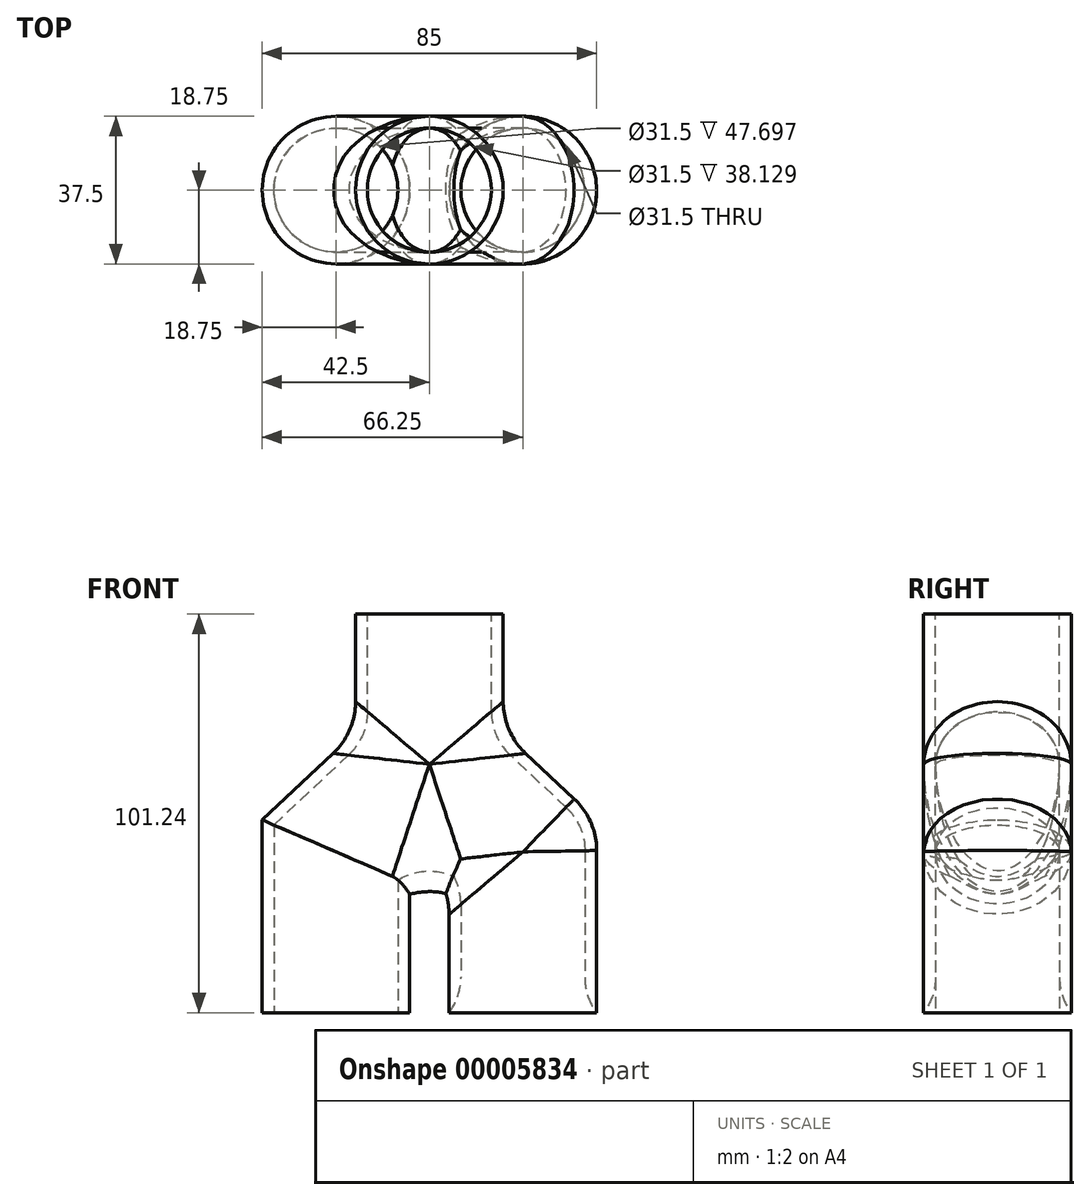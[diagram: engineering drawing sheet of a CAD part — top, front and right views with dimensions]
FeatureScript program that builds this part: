
annotation { "Feature Type Name" : "Feature", "Feature Type Description" : "" }
export const myFeature = defineFeature(function(context is Context, id is Id, definition is map)
    precondition{}
    {
        {
            var Q0;
            Q0=qCreatedBy(makeId("Front.planeOp"),FACE);
            var sketch = newSketch(context, id + "F0", { "sketchPlane" : qUnion([Q0])});
            skLineSegment(sketch, "E0.bottom", {"start": v(-18.75, 66.56) * mm, "end": v(-15.75, 66.56) * mm});
            skLineSegment(sketch, "E0.left", {"start": v(-18.75, 66.56) * mm, "end": v(-18.75, 14.77) * mm});
            skLineSegment(sketch, "E1.top", {"start": v(-42.5, -34.68) * mm, "end": v(-39.5, -34.68) * mm});
            skLineSegment(sketch, "E1.left", {"start": v(-42.5, 14.32) * mm, "end": v(-42.5, -34.68) * mm});
            skLineSegment(sketch, "E1.right", {"start": v(-5, -4.68) * mm, "end": v(-5, -34.68) * mm});
            skLineSegment(sketch, "E2", {"start": v(0, 69.18) * mm, "end": v(0, -67.25) * mm, "construction": true});
            skLineSegment(sketch, "E3.0", {"start": v(-39.5, 13.01) * mm, "end": v(-39.5, -34.68) * mm});
            skLineSegment(sketch, "E3.1", {"start": v(-39.5, 13.01) * mm, "end": v(-15.75, 35.26) * mm});
            skLineSegment(sketch, "E3.2", {"start": v(-15.75, 66.56) * mm, "end": v(-15.75, 14.77) * mm});
            skLineSegment(sketch, "E4.0", {"start": v(-8, -0.64) * mm, "end": v(-8, -34.68) * mm});
            skLineSegment(sketch, "E5", {"start": v(-3.42, 3.65) * mm, "end": v(-8, -0.64) * mm});
            skLineSegment(sketch, "E6", {"start": v(-5, -4.68) * mm, "end": v(0, 0) * mm});
            skArc(sketch, "E7", {"start": v(0, 5) * mm, "mid": v(-1.84, 4.65) * mm, "end": v(-3.42, 3.65) * mm});
            skLineSegment(sketch, "E8.trimOffspring", {"start": v(-8, -34.68) * mm, "end": v(-5, -34.68) * mm});
            skLineSegment(sketch, "E9.MirrorCS", {"start": v(8, -34.68) * mm, "end": v(5, -34.68) * mm});
            skLineSegment(sketch, "E10.MirrorCS", {"start": v(42.5, -34.68) * mm, "end": v(39.5, -34.68) * mm});
            skLineSegment(sketch, "E11.MirrorCS", {"start": v(18.75, 66.56) * mm, "end": v(15.75, 66.56) * mm});
            skArc(sketch, "E12.MirrorCS", {"start": v(0, 5) * mm, "mid": v(1.84, 4.65) * mm, "end": v(3.42, 3.65) * mm});
            skLineSegment(sketch, "E13.MirrorCS", {"start": v(3.42, 3.65) * mm, "end": v(8, -0.64) * mm});
            skLineSegment(sketch, "E14.MirrorCS", {"start": v(8, -0.64) * mm, "end": v(8, -34.68) * mm});
            skLineSegment(sketch, "E15.MirrorCS", {"start": v(15.75, 66.56) * mm, "end": v(15.75, 35.26) * mm});
            skLineSegment(sketch, "E16.MirrorCS", {"start": v(39.5, 13.01) * mm, "end": v(15.75, 35.26) * mm});
            skLineSegment(sketch, "E17.MirrorCS", {"start": v(42.5, 14.32) * mm, "end": v(18.75, 36.56) * mm});
            skLineSegment(sketch, "E18.MirrorCS", {"start": v(5, -4.68) * mm, "end": v(5, -34.68) * mm});
            skLineSegment(sketch, "E19.MirrorCS", {"start": v(42.5, 14.32) * mm, "end": v(42.5, -34.68) * mm});
            skLineSegment(sketch, "E20.MirrorCS", {"start": v(18.75, 66.56) * mm, "end": v(18.75, 36.56) * mm});
            skLineSegment(sketch, "E21.MirrorCS", {"start": v(5, -4.68) * mm, "end": v(0, 0) * mm});
            skLineSegment(sketch, "E22.MirrorCS", {"start": v(39.5, 13.01) * mm, "end": v(39.5, -34.68) * mm});
            skLineSegment(sketch, "E23", {"start": v(0, 0) * mm, "end": v(0, 5) * mm});
            skLineSegment(sketch, "E24", {"start": v(0, 28.43) * mm, "end": v(-56.58, -24.56) * mm, "construction": true});
            skLineSegment(sketch, "E25", {"start": v(0, 28.43) * mm, "end": v(56.54, -24.52) * mm, "construction": true});
            skLineSegment(sketch, "E26", {"start": v(3.42, 3.65) * mm, "end": v(14.18, 15.15) * mm, "construction": true});
            skLineSegment(sketch, "E27", {"start": v(14.18, 15.15) * mm, "end": v(24.95, 26.64) * mm, "construction": true});
            skPoint(sketch, "E28", {"position": v(0, 28.43) * mm});
            skLineSegment(sketch, "E29", {"start": v(-39.5, 13.01) * mm, "end": v(-42.5, 14.32) * mm});
            skLineSegment(sketch, "E30", {"start": v(15.75, 35.26) * mm, "end": v(18.75, 36.56) * mm});
            skLineSegment(sketch, "E31", {"start": v(39.5, 13.01) * mm, "end": v(42.5, 14.32) * mm});
            skLineSegment(sketch, "E32", {"start": v(-23.75, -34.68) * mm, "end": v(-23.75, 15.83) * mm, "construction": true});
            skLineSegment(sketch, "E33", {"start": v(-39.5, -34.68) * mm, "end": v(-23.75, -34.68) * mm, "construction": true});
            skLineSegment(sketch, "E34", {"start": v(-23.75, -34.68) * mm, "end": v(-8, -34.68) * mm, "construction": true});
            skLineSegment(sketch, "E35.MirrorCS", {"start": v(-47.5, 69.18) * mm, "end": v(-47.5, -67.25) * mm, "construction": true});
            skLineSegment(sketch, "E36", {"start": v(8, -34.68) * mm, "end": v(23.75, -34.68) * mm, "construction": true});
            skLineSegment(sketch, "E37", {"start": v(23.75, -34.68) * mm, "end": v(39.5, -34.68) * mm, "construction": true});
            skLineSegment(sketch, "E38", {"start": v(23.75, -34.68) * mm, "end": v(23.75, 14.7) * mm, "construction": true});
            skLineSegment(sketch, "E39", {"start": v(-18.75, 14.77) * mm, "end": v(-15.75, 14.77) * mm});
            skLineSegment(sketch, "E40", {"start": v(-42.5, 14.32) * mm, "end": v(-9.1, 45.59) * mm});
            skLineSegment(sketch, "E41", {"start": v(-9.1, 45.59) * mm, "end": v(-7.06, 43.4) * mm});
            skLineSegment(sketch, "E42", {"start": v(-7.06, 43.4) * mm, "end": v(-15.75, 35.26) * mm});
            skLineSegment(sketch, "E43.MirrorCS", {"start": v(9.1, 45.59) * mm, "end": v(7.06, 43.4) * mm});
            skLineSegment(sketch, "E44.MirrorCS", {"start": v(7.06, 43.4) * mm, "end": v(15.75, 35.26) * mm});
            skLineSegment(sketch, "E45.MirrorCS", {"start": v(42.5, 14.32) * mm, "end": v(9.1, 45.59) * mm});
            skSolve(sketch);
        }
        {
            var Q0;
            Q0=makeQuery(id+"F0.imprint","IMPRINT",FACE,{"disambiguationData":[TD([[makeQuery(id+"F0.imprint","IMPRINT",EDGE,{"derivedFrom":sQuery(id+"F0.wireOp",EDGE,"E0.bottom")}),-1.0]])]});
            var Q1;
            {var subQ0=sQuery(id+"F0.wireOp",EDGE,"xYfYZVj4-OU23-bML6-88x0-pwoqxrOmsgBR");Q1=makeQuery(id+"F0.imprint","IMPRINT",FACE,{"disambiguationData":[TD([[makeQuery(id+"F0.imprint","IMPRINT",EDGE,{"derivedFrom":subQ0}),-1.0]])]});}
            var Q2;
            {var subQ0=sQuery(id+"F0.wireOp",EDGE,"E39");Q2=makeQuery(id+"F0.imprint","IMPRINT",FACE,{"disambiguationData":[TD([[makeQuery(id+"F0.imprint","IMPRINT",EDGE,{"derivedFrom":subQ0}),1.0]])]});}
            var Q3;
            {var subQ0=sQuery(id+"F0.wireOp",EDGE,"E40");var subQ1=sQuery(id+"F0.wireOp",EDGE,"E0.left");var subQ2=makeQuery(id+"F0.imprint","INTERSECT",VERTEX,{"derivedFrom":[subQ1,subQ0]});Q3=makeQuery(id+"F0.imprint","IMPRINT",FACE,{"disambiguationData":[TD([[makeQuery(id+"F0.imprint","IMPRINT",EDGE,{"disambiguationData":[TD([[subQ2,-1.0]])],"derivedFrom":subQ1}),1.0]])]});}
            var Q4;
            Q4=sQuery(id+"F0.wireOp",EDGE,"E2");
            revolve(context, id + "F1", {"surfaceOperationType" : NewSurfaceOperationType.NEW, "entities" : qUnion([Q0, Q1, Q2, Q3]), "axis" : qUnion([Q4]), "revolveType" : RevolveType.FULL});
        }
        {
            var Q0;
            {var subQ5=sQuery(id+"F0.wireOp",EDGE,"E29");Q0=makeQuery(id+"F0.imprint","IMPRINT",FACE,{"disambiguationData":[TD([[makeQuery(id+"F0.imprint","IMPRINT",EDGE,{"derivedFrom":subQ5}),-1.0]])]});}
            var Q1;
            {var subQ0=sQuery(id+"F0.wireOp",EDGE,"E40");var subQ1=sQuery(id+"F0.wireOp",EDGE,"E0.left");var subQ2=makeQuery(id+"F0.imprint","INTERSECT",VERTEX,{"derivedFrom":[subQ1,subQ0]});Q1=makeQuery(id+"F0.imprint","IMPRINT",FACE,{"disambiguationData":[TD([[makeQuery(id+"F0.imprint","IMPRINT",EDGE,{"disambiguationData":[TD([[subQ2,-1.0]])],"derivedFrom":subQ1}),1.0]])]});}
            var Q2;
            {var subQ4=sQuery(id+"F0.wireOp",EDGE,"E41");Q2=makeQuery(id+"F0.imprint","IMPRINT",FACE,{"disambiguationData":[TD([[makeQuery(id+"F0.imprint","IMPRINT",EDGE,{"derivedFrom":subQ4}),-1.0]])]});}
            var Q3;
            Q3=sQuery(id+"F0.wireOp",EDGE,"E24");
            revolve(context, id + "F2", {"surfaceOperationType" : NewSurfaceOperationType.NEW, "entities" : qUnion([Q0, Q1, Q2]), "axis" : qUnion([Q3]), "revolveType" : RevolveType.FULL});
        }
        {
            var Q0;
            Q0=makeQuery(id+"F0.imprint","IMPRINT",FACE,{"disambiguationData":[TD([[makeQuery(id+"F0.imprint","IMPRINT",EDGE,{"derivedFrom":sQuery(id+"F0.wireOp",EDGE,"E1.top")}),1.0]])]});
            var Q1;
            Q1=sQuery(id+"F0.wireOp",EDGE,"E32");
            revolve(context, id + "F3", {"surfaceOperationType" : NewSurfaceOperationType.NEW, "entities" : qUnion([Q0]), "axis" : qUnion([Q1]), "revolveType" : RevolveType.FULL});
        }
        {
            var Q0;
            Q0=qCreatedBy(makeId("Front.planeOp"),FACE);
            var sketch = newSketch(context, id + "F4", { "sketchPlane" : qUnion([Q0])});
            skPoint(sketch, "E46.0", {"position": v(-42.5, 14.32) * mm});
            skLineSegment(sketch, "E47.0", {"start": v(-5, -1.94) * mm, "end": v(-5, -34.68) * mm});
            skPoint(sketch, "E48.orphan", {"position": v(-5, -4.68) * mm});
            skLineSegment(sketch, "E49", {"start": v(-5, -1.94) * mm, "end": v(-42.5, 14.32) * mm});
            skLineSegment(sketch, "E50", {"start": v(-42.5, 14.32) * mm, "end": v(-42.5, -34.68) * mm});
            skLineSegment(sketch, "E51", {"start": v(-42.5, -34.68) * mm, "end": v(-5, -34.68) * mm});
            skLineSegment(sketch, "E52.0", {"start": v(-42.5, 14.32) * mm, "end": v(-18.75, 36.56) * mm});
            skLineSegment(sketch, "E53.0", {"start": v(-18.75, 66.56) * mm, "end": v(-18.75, 36.56) * mm});
            skLineSegment(sketch, "E54.0", {"start": v(13.72, 15.58) * mm, "end": v(14.58, 14.77) * mm});
            skLineSegment(sketch, "E55", {"start": v(-18.75, 36.56) * mm, "end": v(0, 28.43) * mm});
            skLineSegment(sketch, "E56.0", {"start": v(18.75, 66.56) * mm, "end": v(18.75, 36.56) * mm});
            skLineSegment(sketch, "E57", {"start": v(0, 28.43) * mm, "end": v(18.75, 36.56) * mm});
            skPoint(sketch, "E58.orphan", {"position": v(-9.1, 45.59) * mm});
            skLineSegment(sketch, "E59.0", {"start": v(-18.75, 66.56) * mm, "end": v(18.75, 66.56) * mm});
            skLineSegment(sketch, "E60", {"start": v(-18.75, 36.56) * mm, "end": v(-18.75, 66.56) * mm});
            skPoint(sketch, "E61.0.start.orphan", {"position": v(0, 28.43) * mm});
            skPoint(sketch, "E62.orphan", {"position": v(56.54, -24.52) * mm});
            skPoint(sketch, "E63.orphan", {"position": v(0, -67.25) * mm});
            skLineSegment(sketch, "E64.trimOffspring", {"start": v(0, 28.43) * mm, "end": v(0, 2.74) * mm});
            skLineSegment(sketch, "E65.trimOffspring", {"start": v(0, 2.74) * mm, "end": v(-5, -1.94) * mm});
            skPoint(sketch, "E66.0.start.orphan", {"position": v(0, 69.18) * mm});
            skSolve(sketch);
        }
        {
            var Q0;
            Q0=makeQuery(id+"F4.imprint","IMPRINT",FACE,{"disambiguationData":[TD([[makeQuery(id+"F4.imprint","IMPRINT",EDGE,{"derivedFrom":sQuery(id+"F4.wireOp",EDGE,"E55")}),1.0]])]});
            extrude(context, id + "F5", {"entities" : qUnion([Q0]), "endBound" : BoundingType.SYMMETRIC, "depth" : 40 * mm, "offsetDistance" : 25 * mm});
        }
        {
            var Q0;
            Q0=makeQuery(id+"F4.imprint","IMPRINT",FACE,{"disambiguationData":[TD([[makeQuery(id+"F4.imprint","IMPRINT",EDGE,{"derivedFrom":sQuery(id+"F4.wireOp",EDGE,"E49")}),-1.0]])]});
            extrude(context, id + "F6", {"entities" : qUnion([Q0]), "endBound" : BoundingType.SYMMETRIC, "depth" : 40 * mm, "offsetDistance" : 25 * mm});
        }
        {
            var Q0;
            Q0=makeQuery(id+"F4.imprint","IMPRINT",FACE,{"disambiguationData":[TD([[makeQuery(id+"F4.imprint","IMPRINT",EDGE,{"derivedFrom":sQuery(id+"F4.wireOp",EDGE,"E47.0")}),-1.0]])]});
            extrude(context, id + "F7", {"entities" : qUnion([Q0]), "endBound" : BoundingType.SYMMETRIC, "depth" : 40 * mm, "offsetDistance" : 25 * mm});
        }
        {
            var Q0;
            Q0=makeQuery(id+"F1.opRevolve","SWEPT_BODY",BODY,{"disambiguationData":[OSD([sQuery(id+"F0.wireOp",EDGE,"E0.bottom"),sQuery(id+"F0.wireOp",EDGE,"E0.left"),sQuery(id+"F0.wireOp",EDGE,"E3.2"),sQuery(id+"F0.wireOp",EDGE,"E39")])]});
            var Q1;
            Q1=makeQuery(id+"F5.opExtrude","SWEPT_BODY",BODY,{"disambiguationData":[OSD([sQuery(id+"F4.wireOp",EDGE,"E55"),sQuery(id+"F4.wireOp",EDGE,"E56.0"),sQuery(id+"F4.wireOp",EDGE,"E57"),sQuery(id+"F4.wireOp",EDGE,"E59.0"),sQuery(id+"F4.wireOp",EDGE,"E60")])]});
            booleanBodies(context, id + "F8", {"operationType" : BooleanOperationType.INTERSECTION, "tools" : qUnion([Q0, Q1])});
        }
        {
            var Q0;
            Q0=makeQuery(id+"F6.opExtrude","SWEPT_BODY",BODY,{"disambiguationData":[OSD([sQuery(id+"F4.wireOp",EDGE,"E49"),sQuery(id+"F4.wireOp",EDGE,"E52.0"),sQuery(id+"F4.wireOp",EDGE,"E55"),sQuery(id+"F4.wireOp",EDGE,"E64.trimOffspring"),sQuery(id+"F4.wireOp",EDGE,"E65.trimOffspring")])]});
            var Q1;
            Q1=makeQuery(id+"F2.opRevolve","SWEPT_BODY",BODY,{"disambiguationData":[OSD([sQuery(id+"F0.wireOp",EDGE,"E3.1"),sQuery(id+"F0.wireOp",EDGE,"E29"),sQuery(id+"F0.wireOp",EDGE,"E40"),sQuery(id+"F0.wireOp",EDGE,"E41"),sQuery(id+"F0.wireOp",EDGE,"E42")])]});
            booleanBodies(context, id + "F9", {"operationType" : BooleanOperationType.INTERSECTION, "tools" : qUnion([Q0, Q1])});
        }
        {
            var Q0;
            Q0=makeQuery(id+"F3.opRevolve","SWEPT_BODY",BODY,{"disambiguationData":[OSD([sQuery(id+"F0.wireOp",EDGE,"E1.top"),sQuery(id+"F0.wireOp",EDGE,"E1.left"),sQuery(id+"F0.wireOp",EDGE,"E3.0"),sQuery(id+"F0.wireOp",EDGE,"E29")])]});
            var Q1;
            Q1=makeQuery(id+"F7.opExtrude","SWEPT_BODY",BODY,{"disambiguationData":[OSD([sQuery(id+"F4.wireOp",EDGE,"E47.0"),sQuery(id+"F4.wireOp",EDGE,"E49"),sQuery(id+"F4.wireOp",EDGE,"E50"),sQuery(id+"F4.wireOp",EDGE,"E51")])]});
            booleanBodies(context, id + "F10", {"operationType" : BooleanOperationType.INTERSECTION, "tools" : qUnion([Q0, Q1])});
        }
        {
            var Q0;
            Q0=makeQuery(id+"F9.opBoolean","INTERSECT",BODY,{"derivedFrom":[makeQuery(id+"F2.opRevolve","SWEPT_BODY",BODY,{"disambiguationData":[OSD([sQuery(id+"F0.wireOp",EDGE,"E3.1"),sQuery(id+"F0.wireOp",EDGE,"E29"),sQuery(id+"F0.wireOp",EDGE,"E40"),sQuery(id+"F0.wireOp",EDGE,"E41"),sQuery(id+"F0.wireOp",EDGE,"E42")])]}),makeQuery(id+"F6.opExtrude","SWEPT_BODY",BODY,{"disambiguationData":[OSD([sQuery(id+"F4.wireOp",EDGE,"E49"),sQuery(id+"F4.wireOp",EDGE,"E52.0"),sQuery(id+"F4.wireOp",EDGE,"E55"),sQuery(id+"F4.wireOp",EDGE,"E64.trimOffspring"),sQuery(id+"F4.wireOp",EDGE,"E65.trimOffspring")])]})]});
            var Q1;
            Q1=qCreatedBy(makeId("Right.planeOp"),FACE);
            mirror(context, id + "F11", {"entities" : qUnion([Q0]), "mirrorPlane" : qUnion([Q1])});
        }
        {
            var Q0;
            Q0=makeQuery(id+"F10.opBoolean","INTERSECT",BODY,{"derivedFrom":[makeQuery(id+"F3.opRevolve","SWEPT_BODY",BODY,{"disambiguationData":[OSD([sQuery(id+"F0.wireOp",EDGE,"E1.top"),sQuery(id+"F0.wireOp",EDGE,"E1.left"),sQuery(id+"F0.wireOp",EDGE,"E3.0"),sQuery(id+"F0.wireOp",EDGE,"E29")])]}),makeQuery(id+"F7.opExtrude","SWEPT_BODY",BODY,{"disambiguationData":[OSD([sQuery(id+"F4.wireOp",EDGE,"E47.0"),sQuery(id+"F4.wireOp",EDGE,"E49"),sQuery(id+"F4.wireOp",EDGE,"E50"),sQuery(id+"F4.wireOp",EDGE,"E51")])]})]});
            var Q1;
            Q1=qCreatedBy(makeId("Right.planeOp"),FACE);
            mirror(context, id + "F12", {"operationType" : NewBodyOperationType.ADD, "entities" : qUnion([Q0]), "mirrorPlane" : qUnion([Q1])});
        }
        {
            var Q0;
            Q0=makeQuery(id+"F9.opBoolean","INTERSECT",BODY,{"derivedFrom":[makeQuery(id+"F2.opRevolve","SWEPT_BODY",BODY,{"disambiguationData":[OSD([sQuery(id+"F0.wireOp",EDGE,"E3.1"),sQuery(id+"F0.wireOp",EDGE,"E29"),sQuery(id+"F0.wireOp",EDGE,"E40"),sQuery(id+"F0.wireOp",EDGE,"E41"),sQuery(id+"F0.wireOp",EDGE,"E42")])]}),makeQuery(id+"F6.opExtrude","SWEPT_BODY",BODY,{"disambiguationData":[OSD([sQuery(id+"F4.wireOp",EDGE,"E49"),sQuery(id+"F4.wireOp",EDGE,"E52.0"),sQuery(id+"F4.wireOp",EDGE,"E55"),sQuery(id+"F4.wireOp",EDGE,"E64.trimOffspring"),sQuery(id+"F4.wireOp",EDGE,"E65.trimOffspring")])]})]});
            var Q1;
            Q1=makeQuery(id+"F10.opBoolean","INTERSECT",BODY,{"derivedFrom":[makeQuery(id+"F3.opRevolve","SWEPT_BODY",BODY,{"disambiguationData":[OSD([sQuery(id+"F0.wireOp",EDGE,"E1.top"),sQuery(id+"F0.wireOp",EDGE,"E1.left"),sQuery(id+"F0.wireOp",EDGE,"E3.0"),sQuery(id+"F0.wireOp",EDGE,"E29")])]}),makeQuery(id+"F7.opExtrude","SWEPT_BODY",BODY,{"disambiguationData":[OSD([sQuery(id+"F4.wireOp",EDGE,"E47.0"),sQuery(id+"F4.wireOp",EDGE,"E49"),sQuery(id+"F4.wireOp",EDGE,"E50"),sQuery(id+"F4.wireOp",EDGE,"E51")])]})]});
            var Q2;
            Q2=makeQuery(id+"F8.opBoolean","INTERSECT",BODY,{"derivedFrom":[makeQuery(id+"F1.opRevolve","SWEPT_BODY",BODY,{"disambiguationData":[OSD([sQuery(id+"F0.wireOp",EDGE,"E0.bottom"),sQuery(id+"F0.wireOp",EDGE,"E0.left"),sQuery(id+"F0.wireOp",EDGE,"E3.2"),sQuery(id+"F0.wireOp",EDGE,"E39")])]}),makeQuery(id+"F5.opExtrude","SWEPT_BODY",BODY,{"disambiguationData":[OSD([sQuery(id+"F4.wireOp",EDGE,"E55"),sQuery(id+"F4.wireOp",EDGE,"E56.0"),sQuery(id+"F4.wireOp",EDGE,"E57"),sQuery(id+"F4.wireOp",EDGE,"E59.0"),sQuery(id+"F4.wireOp",EDGE,"E60")])]})]});
            var Q3;
            Q3=makeQuery(id+"F11.opPattern","COPY",BODY,{"derivedFrom":makeQuery(id+"F9.opBoolean","INTERSECT",BODY,{"derivedFrom":[makeQuery(id+"F2.opRevolve","SWEPT_BODY",BODY,{"disambiguationData":[OSD([sQuery(id+"F0.wireOp",EDGE,"E3.1"),sQuery(id+"F0.wireOp",EDGE,"E29"),sQuery(id+"F0.wireOp",EDGE,"E40"),sQuery(id+"F0.wireOp",EDGE,"E41"),sQuery(id+"F0.wireOp",EDGE,"E42")])]}),makeQuery(id+"F6.opExtrude","SWEPT_BODY",BODY,{"disambiguationData":[OSD([sQuery(id+"F4.wireOp",EDGE,"E49"),sQuery(id+"F4.wireOp",EDGE,"E52.0"),sQuery(id+"F4.wireOp",EDGE,"E55"),sQuery(id+"F4.wireOp",EDGE,"E64.trimOffspring"),sQuery(id+"F4.wireOp",EDGE,"E65.trimOffspring")])]})]}),"instanceName":"1"});
            booleanBodies(context, id + "F13", {"operationType" : BooleanOperationType.UNION, "tools" : qUnion([Q0, Q1, Q2, Q3])});
        }
        {
            var Q0;
            {var subQ0=sQuery(id+"F4.wireOp",EDGE,"E49");Q0=makeQuery(id+"F13.opBoolean","MERGE",EDGE,{"derivedFrom":[makeQuery(id+"F9.opBoolean","INTERSECT",EDGE,{"derivedFrom":[makeQuery(id+"F2.opRevolve","SWEPT_FACE",FACE,{"disambiguationData":[OSD([sQuery(id+"F0.wireOp",EDGE,"E40")])]}),makeQuery(id+"F6.opExtrude","SWEPT_FACE",FACE,{"disambiguationData":[OSD([subQ0])]})]}),makeQuery(id+"F10.opBoolean","INTERSECT",EDGE,{"derivedFrom":[makeQuery(id+"F3.opRevolve","SWEPT_FACE",FACE,{"disambiguationData":[OSD([sQuery(id+"F0.wireOp",EDGE,"E1.left")])]}),makeQuery(id+"F7.opExtrude","SWEPT_FACE",FACE,{"disambiguationData":[OSD([subQ0])]})]})]});}
            var Q1;
            {var subQ0=sQuery(id+"F4.wireOp",EDGE,"E49");Q1=makeQuery(id+"F12.boolean.opBoolean","MERGE",EDGE,{"derivedFrom":[makeQuery(id+"F11.opPattern","COPY",EDGE,{"derivedFrom":makeQuery(id+"F9.opBoolean","INTERSECT",EDGE,{"derivedFrom":[makeQuery(id+"F2.opRevolve","SWEPT_FACE",FACE,{"disambiguationData":[OSD([sQuery(id+"F0.wireOp",EDGE,"E40")])]}),makeQuery(id+"F6.opExtrude","SWEPT_FACE",FACE,{"disambiguationData":[OSD([subQ0])]})]}),"instanceName":"1"}),makeQuery(id+"F12.opPattern","COPY",EDGE,{"derivedFrom":makeQuery(id+"F10.opBoolean","INTERSECT",EDGE,{"derivedFrom":[makeQuery(id+"F3.opRevolve","SWEPT_FACE",FACE,{"disambiguationData":[OSD([sQuery(id+"F0.wireOp",EDGE,"E1.left")])]}),makeQuery(id+"F7.opExtrude","SWEPT_FACE",FACE,{"disambiguationData":[OSD([subQ0])]})]}),"instanceName":"1"})]});}
            var Q2;
            Q2=makeQuery(id+"F13.opBoolean","MERGE",EDGE,{"derivedFrom":[makeQuery(id+"F8.opBoolean","INTERSECT",EDGE,{"derivedFrom":[makeQuery(id+"F1.opRevolve","SWEPT_FACE",FACE,{"disambiguationData":[OSD([sQuery(id+"F0.wireOp",EDGE,"E0.left")])]}),makeQuery(id+"F5.opExtrude","SWEPT_FACE",FACE,{"disambiguationData":[OSD([sQuery(id+"F4.wireOp",EDGE,"E57")])]})]}),makeQuery(id+"F11.opPattern","COPY",EDGE,{"derivedFrom":makeQuery(id+"F9.opBoolean","INTERSECT",EDGE,{"derivedFrom":[makeQuery(id+"F2.opRevolve","SWEPT_FACE",FACE,{"disambiguationData":[OSD([sQuery(id+"F0.wireOp",EDGE,"E40")])]}),makeQuery(id+"F6.opExtrude","SWEPT_FACE",FACE,{"disambiguationData":[OSD([sQuery(id+"F4.wireOp",EDGE,"E55")])]})]}),"instanceName":"1"})]});
            var Q3;
            {var subQ0=sQuery(id+"F4.wireOp",EDGE,"E55");Q3=makeQuery(id+"F13.opBoolean","MERGE",EDGE,{"derivedFrom":[makeQuery(id+"F8.opBoolean","INTERSECT",EDGE,{"derivedFrom":[makeQuery(id+"F1.opRevolve","SWEPT_FACE",FACE,{"disambiguationData":[OSD([sQuery(id+"F0.wireOp",EDGE,"E0.left")])]}),makeQuery(id+"F5.opExtrude","SWEPT_FACE",FACE,{"disambiguationData":[OSD([subQ0])]})]}),makeQuery(id+"F9.opBoolean","INTERSECT",EDGE,{"derivedFrom":[makeQuery(id+"F2.opRevolve","SWEPT_FACE",FACE,{"disambiguationData":[OSD([sQuery(id+"F0.wireOp",EDGE,"E40")])]}),makeQuery(id+"F6.opExtrude","SWEPT_FACE",FACE,{"disambiguationData":[OSD([subQ0])]})]})]});}
            var Q4;
            {var subQ0=makeQuery(id+"F9.opBoolean","INTERSECT",EDGE,{"derivedFrom":[makeQuery(id+"F2.opRevolve","SWEPT_FACE",FACE,{"disambiguationData":[OSD([sQuery(id+"F0.wireOp",EDGE,"E40")])]}),makeQuery(id+"F6.opExtrude","SWEPT_FACE",FACE,{"disambiguationData":[OSD([sQuery(id+"F4.wireOp",EDGE,"E64.trimOffspring")])]})]});Q4=makeQuery(id+"F13.opBoolean","MERGE",EDGE,{"derivedFrom":[subQ0,makeQuery(id+"F11.opPattern","COPY",EDGE,{"derivedFrom":subQ0,"instanceName":"1"})]});}
            fillet(context, id + "F14", {"entities" : qUnion([Q0, Q1, Q2, Q3, Q4]), "radius" : 18 * mm, "tangentPropagation" : true, "allowEdgeOverflow" : false});
        }
        {
            var Q0;
            {var subQ0=sQuery(id+"F4.wireOp",EDGE,"E49");Q0=makeQuery(id+"F13.opBoolean","MERGE",EDGE,{"derivedFrom":[makeQuery(id+"F9.opBoolean","INTERSECT",EDGE,{"derivedFrom":[makeQuery(id+"F2.opRevolve","SWEPT_FACE",FACE,{"disambiguationData":[OSD([sQuery(id+"F0.wireOp",EDGE,"E3.1"),sQuery(id+"F0.wireOp",EDGE,"E42")])]}),makeQuery(id+"F6.opExtrude","SWEPT_FACE",FACE,{"disambiguationData":[OSD([subQ0])]})]}),makeQuery(id+"F10.opBoolean","INTERSECT",EDGE,{"derivedFrom":[makeQuery(id+"F3.opRevolve","SWEPT_FACE",FACE,{"disambiguationData":[OSD([sQuery(id+"F0.wireOp",EDGE,"E3.0")])]}),makeQuery(id+"F7.opExtrude","SWEPT_FACE",FACE,{"disambiguationData":[OSD([subQ0])]})]})]});}
            var Q1;
            Q1=makeQuery(id+"F12.opPattern","COPY",FACE,{"derivedFrom":makeQuery(id+"F3.opRevolve","SWEPT_FACE",FACE,{"disambiguationData":[OSD([sQuery(id+"F0.wireOp",EDGE,"E3.0")])]}),"instanceName":"1"});
            var Q2;
            {var subQ0=sQuery(id+"F4.wireOp",EDGE,"E55");Q2=makeQuery(id+"F13.opBoolean","MERGE",EDGE,{"derivedFrom":[makeQuery(id+"F8.opBoolean","INTERSECT",EDGE,{"derivedFrom":[makeQuery(id+"F1.opRevolve","SWEPT_FACE",FACE,{"disambiguationData":[OSD([sQuery(id+"F0.wireOp",EDGE,"E3.2")])]}),makeQuery(id+"F5.opExtrude","SWEPT_FACE",FACE,{"disambiguationData":[OSD([subQ0])]})]}),makeQuery(id+"F9.opBoolean","INTERSECT",EDGE,{"derivedFrom":[makeQuery(id+"F2.opRevolve","SWEPT_FACE",FACE,{"disambiguationData":[OSD([sQuery(id+"F0.wireOp",EDGE,"E3.1"),sQuery(id+"F0.wireOp",EDGE,"E42")])]}),makeQuery(id+"F6.opExtrude","SWEPT_FACE",FACE,{"disambiguationData":[OSD([subQ0])]})]})]});}
            var Q3;
            Q3=makeQuery(id+"F13.opBoolean","MERGE",EDGE,{"derivedFrom":[makeQuery(id+"F8.opBoolean","INTERSECT",EDGE,{"derivedFrom":[makeQuery(id+"F1.opRevolve","SWEPT_FACE",FACE,{"disambiguationData":[OSD([sQuery(id+"F0.wireOp",EDGE,"E3.2")])]}),makeQuery(id+"F5.opExtrude","SWEPT_FACE",FACE,{"disambiguationData":[OSD([sQuery(id+"F4.wireOp",EDGE,"E57")])]})]}),makeQuery(id+"F11.opPattern","COPY",EDGE,{"derivedFrom":makeQuery(id+"F9.opBoolean","INTERSECT",EDGE,{"derivedFrom":[makeQuery(id+"F2.opRevolve","SWEPT_FACE",FACE,{"disambiguationData":[OSD([sQuery(id+"F0.wireOp",EDGE,"E3.1"),sQuery(id+"F0.wireOp",EDGE,"E42")])]}),makeQuery(id+"F6.opExtrude","SWEPT_FACE",FACE,{"disambiguationData":[OSD([sQuery(id+"F4.wireOp",EDGE,"E55")])]})]}),"instanceName":"1"})]});
            var Q4;
            {var subQ0=makeQuery(id+"F9.opBoolean","INTERSECT",EDGE,{"derivedFrom":[makeQuery(id+"F2.opRevolve","SWEPT_FACE",FACE,{"disambiguationData":[OSD([sQuery(id+"F0.wireOp",EDGE,"E3.1"),sQuery(id+"F0.wireOp",EDGE,"E42")])]}),makeQuery(id+"F6.opExtrude","SWEPT_FACE",FACE,{"disambiguationData":[OSD([sQuery(id+"F4.wireOp",EDGE,"E64.trimOffspring")])]})]});Q4=makeQuery(id+"F13.opBoolean","MERGE",EDGE,{"derivedFrom":[subQ0,makeQuery(id+"F11.opPattern","COPY",EDGE,{"derivedFrom":subQ0,"instanceName":"1"})]});}
            fillet(context, id + "F15", {"entities" : qUnion([Q0, Q1, Q2, Q3, Q4]), "radius" : 15 * mm, "tangentPropagation" : true, "allowEdgeOverflow" : false});
        }
    });
